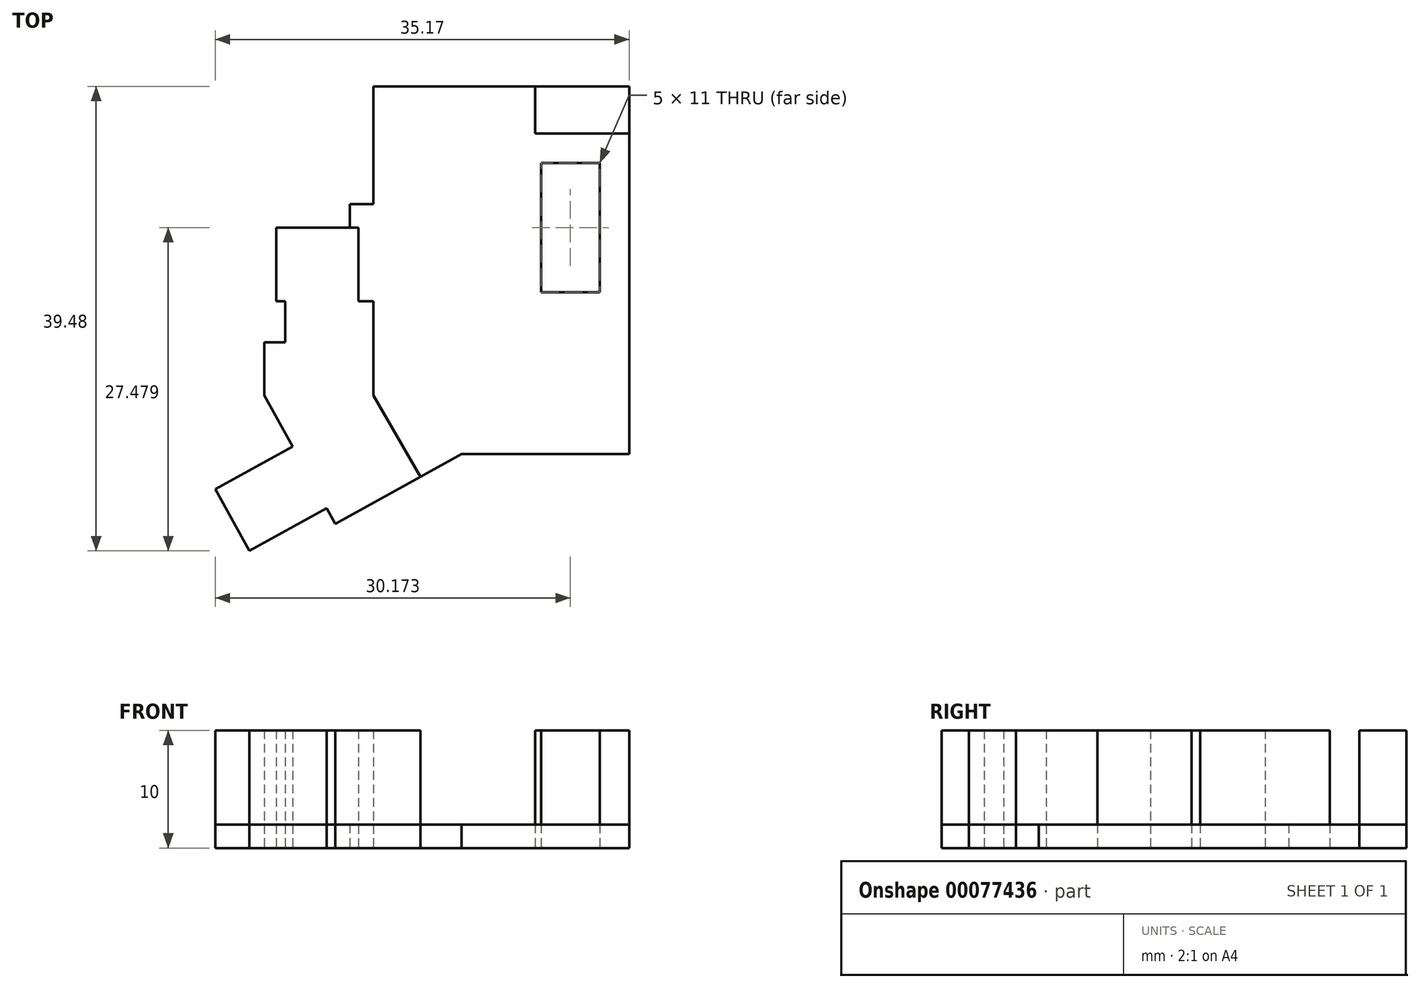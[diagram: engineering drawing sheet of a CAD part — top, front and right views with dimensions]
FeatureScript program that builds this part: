
annotation { "Feature Type Name" : "Feature", "Feature Type Description" : "" }
export const myFeature = defineFeature(function(context is Context, id is Id, definition is map)
    precondition{}
    {
        {
            var Q0;
            Q0=qCreatedBy(makeId("Top.planeOp"),FACE);
            var sketch = newSketch(context, id + "F0", { "sketchPlane" : qUnion([Q0])});
            skLineSegment(sketch, "E0.bottom", {"start": v(-39.18, 26.53) * mm, "end": v(48.82, 26.53) * mm});
            skLineSegment(sketch, "E0.top", {"start": v(-19.18, -18.7) * mm, "end": v(44.44, -18.7) * mm});
            skLineSegment(sketch, "E1", {"start": v(44.44, -18.7) * mm, "end": v(48.82, 26.53) * mm});
            skLineSegment(sketch, "E2", {"start": v(-39.18, 26.53) * mm, "end": v(-45.69, -40.66) * mm});
            skLineSegment(sketch, "E3", {"start": v(-45.69, -40.66) * mm, "end": v(-21.31, -40.66) * mm});
            skLineSegment(sketch, "E4", {"start": v(-21.31, -40.66) * mm, "end": v(-19.18, -18.7) * mm});
            skLineSegment(sketch, "E5.bottom", {"start": v(-33.08, 6.53) * mm, "end": v(-26.08, 6.53) * mm});
            skLineSegment(sketch, "E5.top", {"start": v(-33.08, 0.28) * mm, "end": v(-26.08, 0.28) * mm});
            skLineSegment(sketch, "E5.left", {"start": v(-33.08, 6.53) * mm, "end": v(-33.08, 0.28) * mm});
            skLineSegment(sketch, "E5.right", {"start": v(-26.08, 6.53) * mm, "end": v(-26.08, 0.28) * mm});
            skLineSegment(sketch, "E6.bottom", {"start": v(-32.33, 0.28) * mm, "end": v(-24.83, 0.28) * mm});
            skLineSegment(sketch, "E6.top", {"start": v(-32.33, -7.72) * mm, "end": v(-24.83, -7.72) * mm});
            skLineSegment(sketch, "E6.left", {"start": v(-32.33, 0.28) * mm, "end": v(-32.33, -7.72) * mm});
            skLineSegment(sketch, "E6.right", {"start": v(-24.83, 0.28) * mm, "end": v(-24.83, -7.72) * mm});
            skLineSegment(sketch, "E7.bottom", {"start": v(-32.33, -7.72) * mm, "end": v(-34.08, -7.72) * mm});
            skLineSegment(sketch, "E7.top", {"start": v(-32.33, -3.22) * mm, "end": v(-34.08, -3.22) * mm});
            skLineSegment(sketch, "E7.left", {"start": v(-32.33, -7.72) * mm, "end": v(-32.33, -3.22) * mm});
            skLineSegment(sketch, "E7.right", {"start": v(-34.08, -7.72) * mm, "end": v(-34.08, -3.22) * mm});
            skLineSegment(sketch, "E8", {"start": v(-31.68, -12.07) * mm, "end": v(-38.25, -15.7) * mm});
            skLineSegment(sketch, "E9", {"start": v(-38.25, -15.7) * mm, "end": v(-35.35, -20.95) * mm});
            skLineSegment(sketch, "E10", {"start": v(-35.35, -20.95) * mm, "end": v(-28.78, -17.32) * mm});
            skLineSegment(sketch, "E11", {"start": v(-24.83, -7.72) * mm, "end": v(-20.83, -14.65) * mm});
            skLineSegment(sketch, "E12", {"start": v(-20.83, -14.65) * mm, "end": v(-28.06, -18.64) * mm});
            skLineSegment(sketch, "E13", {"start": v(-28.06, -18.64) * mm, "end": v(-28.78, -17.32) * mm});
            skLineSegment(sketch, "E14", {"start": v(-28.78, -17.32) * mm, "end": v(-31.68, -12.07) * mm});
            skLineSegment(sketch, "E15", {"start": v(-31.68, -12.07) * mm, "end": v(-34.08, -7.72) * mm});
            skLineSegment(sketch, "E16.bottom", {"start": v(-11.08, 18.53) * mm, "end": v(-3.08, 18.53) * mm});
            skLineSegment(sketch, "E16.top", {"start": v(-11.08, 14.53) * mm, "end": v(-3.08, 14.53) * mm});
            skLineSegment(sketch, "E16.left", {"start": v(-11.08, 18.53) * mm, "end": v(-11.08, 14.53) * mm});
            skLineSegment(sketch, "E16.right", {"start": v(-3.08, 18.53) * mm, "end": v(-3.08, 14.53) * mm});
            skLineSegment(sketch, "E17.bottom", {"start": v(-10.58, 12.03) * mm, "end": v(-5.58, 12.03) * mm});
            skLineSegment(sketch, "E17.top", {"start": v(-10.58, 1.03) * mm, "end": v(-5.58, 1.03) * mm});
            skLineSegment(sketch, "E17.left", {"start": v(-10.58, 12.03) * mm, "end": v(-10.58, 1.03) * mm});
            skLineSegment(sketch, "E17.right", {"start": v(-5.58, 12.03) * mm, "end": v(-5.58, 1.03) * mm});
            skSolve(sketch);
        }
        {
            var Q0;
            Q0=makeQuery(id+"F0.imprint","IMPRINT",FACE,{"disambiguationData":[TD([[makeQuery(id+"F0.imprint","IMPRINT",EDGE,{"derivedFrom":sQuery(id+"F0.wireOp",EDGE,"E5.bottom")}),-1.0]])]});
            var Q1;
            Q1=makeQuery(id+"F0.imprint","IMPRINT",FACE,{"disambiguationData":[TD([[makeQuery(id+"F0.imprint","IMPRINT",EDGE,{"derivedFrom":sQuery(id+"F0.wireOp",EDGE,"E6.top")}),1.0]])]});
            var Q2;
            Q2=makeQuery(id+"F0.imprint","IMPRINT",FACE,{"disambiguationData":[TD([[makeQuery(id+"F0.imprint","IMPRINT",EDGE,{"derivedFrom":sQuery(id+"F0.wireOp",EDGE,"E7.bottom")}),-1.0]])]});
            var Q3;
            Q3=makeQuery(id+"F0.imprint","IMPRINT",FACE,{"disambiguationData":[TD([[makeQuery(id+"F0.imprint","IMPRINT",EDGE,{"derivedFrom":sQuery(id+"F0.wireOp",EDGE,"E6.top")}),-1.0]])]});
            var Q4;
            Q4=makeQuery(id+"F0.imprint","IMPRINT",FACE,{"disambiguationData":[TD([[makeQuery(id+"F0.imprint","IMPRINT",EDGE,{"derivedFrom":sQuery(id+"F0.wireOp",EDGE,"E8")}),1.0]])]});
            var Q5;
            Q5=makeQuery(id+"F0.imprint","IMPRINT",FACE,{"disambiguationData":[TD([[makeQuery(id+"F0.imprint","IMPRINT",EDGE,{"derivedFrom":sQuery(id+"F0.wireOp",EDGE,"E16.bottom")}),-1.0]])]});
            var Q6;
            Q6=makeQuery(id+"F0.imprint","IMPRINT",FACE,{"disambiguationData":[TD([[makeQuery(id+"F0.imprint","IMPRINT",EDGE,{"derivedFrom":sQuery(id+"F0.wireOp",EDGE,"E17.bottom")}),-1.0]])]});
            extrude(context, id + "F1", {"entities" : qUnion([Q0, Q1, Q2, Q3, Q4, Q5, Q6]), "depth" : 10 * mm});
        }
        {
            var Q0;
            Q0=qCreatedBy(makeId("Top.planeOp"),FACE);
            var sketch = newSketch(context, id + "F2", { "sketchPlane" : qUnion([Q0])});
            skLineSegment(sketch, "E18.0.0", {"start": v(-35.35, -20.95) * mm, "end": v(-28.78, -17.32) * mm});
            skLineSegment(sketch, "E18.0.1", {"start": v(-28.78, -17.32) * mm, "end": v(-28.06, -18.64) * mm});
            skLineSegment(sketch, "E18.0.2", {"start": v(-28.06, -18.64) * mm, "end": v(-20.83, -14.65) * mm});
            skLineSegment(sketch, "E18.0.3", {"start": v(-20.83, -14.65) * mm, "end": v(-24.83, -7.72) * mm});
            skLineSegment(sketch, "E18.0.4", {"start": v(-24.83, -7.72) * mm, "end": v(-24.83, 0.28) * mm});
            skLineSegment(sketch, "E18.0.5", {"start": v(-24.83, 0.28) * mm, "end": v(-26.08, 0.28) * mm});
            skLineSegment(sketch, "E18.0.6", {"start": v(-26.08, 0.28) * mm, "end": v(-26.08, 6.53) * mm});
            skLineSegment(sketch, "E18.0.7", {"start": v(-26.08, 6.53) * mm, "end": v(-33.08, 6.53) * mm});
            skLineSegment(sketch, "E18.0.8", {"start": v(-33.08, 6.53) * mm, "end": v(-33.08, 0.28) * mm});
            skLineSegment(sketch, "E18.0.9", {"start": v(-33.08, 0.28) * mm, "end": v(-32.33, 0.28) * mm});
            skLineSegment(sketch, "E18.0.10", {"start": v(-32.33, 0.28) * mm, "end": v(-32.33, -3.22) * mm});
            skLineSegment(sketch, "E18.0.11", {"start": v(-32.33, -3.22) * mm, "end": v(-34.08, -3.22) * mm});
            skLineSegment(sketch, "E18.0.12", {"start": v(-34.08, -3.22) * mm, "end": v(-34.08, -7.72) * mm});
            skLineSegment(sketch, "E18.0.13", {"start": v(-34.08, -7.72) * mm, "end": v(-31.68, -12.07) * mm});
            skLineSegment(sketch, "E18.0.14", {"start": v(-31.68, -12.07) * mm, "end": v(-38.25, -15.7) * mm});
            skLineSegment(sketch, "E18.0.15", {"start": v(-38.25, -15.7) * mm, "end": v(-35.35, -20.95) * mm});
            skLineSegment(sketch, "E19.0.0", {"start": v(-5.58, 12.03) * mm, "end": v(-10.58, 12.03) * mm});
            skLineSegment(sketch, "E19.0.1", {"start": v(-10.58, 12.03) * mm, "end": v(-10.58, 1.03) * mm});
            skLineSegment(sketch, "E19.0.2", {"start": v(-10.58, 1.03) * mm, "end": v(-5.58, 1.03) * mm});
            skLineSegment(sketch, "E19.0.3", {"start": v(-5.58, 1.03) * mm, "end": v(-5.58, 12.03) * mm});
            skLineSegment(sketch, "E20.0.0", {"start": v(-3.08, 18.53) * mm, "end": v(-11.08, 18.53) * mm});
            skLineSegment(sketch, "E20.0.1", {"start": v(-11.08, 18.53) * mm, "end": v(-11.08, 14.53) * mm});
            skLineSegment(sketch, "E20.0.2", {"start": v(-11.08, 14.53) * mm, "end": v(-3.08, 14.53) * mm});
            skLineSegment(sketch, "E20.0.3", {"start": v(-3.08, 14.53) * mm, "end": v(-3.08, 18.53) * mm});
            skLineSegment(sketch, "E21", {"start": v(-20.83, -14.65) * mm, "end": v(-17.32, -12.72) * mm, "construction": true});
            skLineSegment(sketch, "E22.top", {"start": v(-3.08, -12.72) * mm, "end": v(-17.32, -12.72) * mm});
            skLineSegment(sketch, "E22.left", {"start": v(-3.08, 18.53) * mm, "end": v(-3.08, -12.72) * mm});
            skLineSegment(sketch, "E23", {"start": v(-17.32, -12.72) * mm, "end": v(-20.83, -14.65) * mm});
            skLineSegment(sketch, "E24", {"start": v(-26.08, 6.53) * mm, "end": v(-26.92, 6.53) * mm});
            skLineSegment(sketch, "E25", {"start": v(-24.83, 8.53) * mm, "end": v(-26.83, 8.53) * mm});
            skLineSegment(sketch, "E26", {"start": v(-26.83, 8.53) * mm, "end": v(-26.83, 6.53) * mm});
            skLineSegment(sketch, "E27", {"start": v(-26.83, 6.53) * mm, "end": v(-26.08, 6.53) * mm});
            skLineSegment(sketch, "E28", {"start": v(-3.08, 18.53) * mm, "end": v(-24.83, 18.53) * mm});
            skLineSegment(sketch, "E29", {"start": v(-24.83, 18.53) * mm, "end": v(-24.83, 8.53) * mm});
            skSolve(sketch);
        }
        {
            var Q0;
            Q0=qSketchRegion(id+"F2",true);
            extrude(context, id + "F3", {"entities" : qUnion([Q0]), "depth" : 2 * mm});
        }
    });
